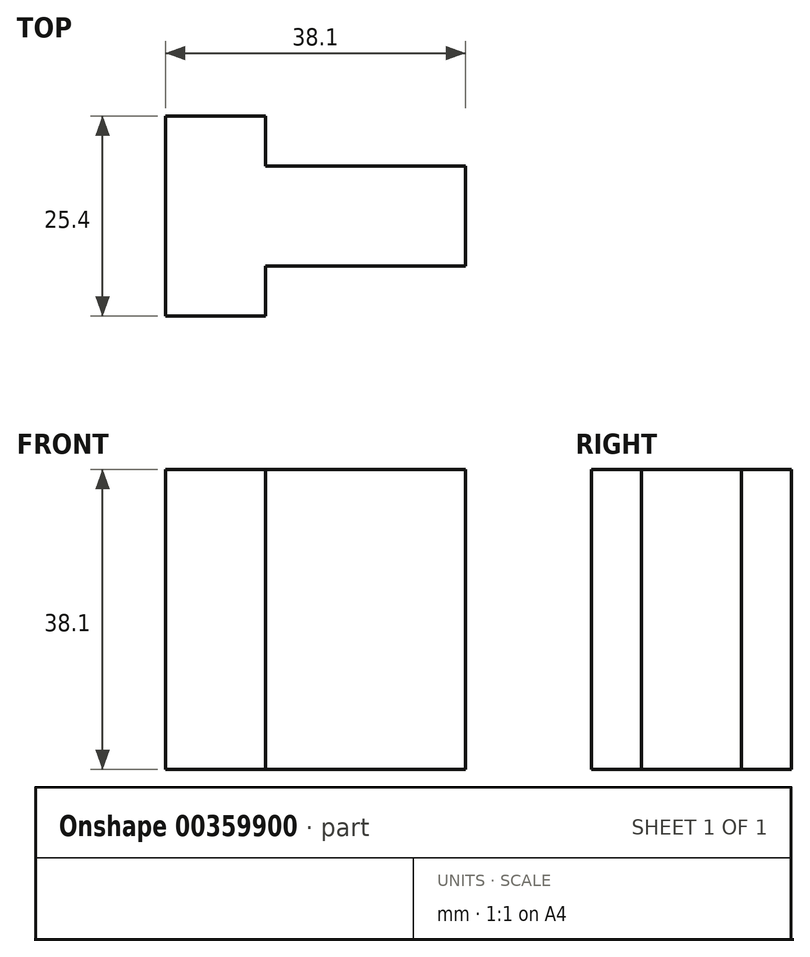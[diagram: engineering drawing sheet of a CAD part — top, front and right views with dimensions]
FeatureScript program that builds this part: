
annotation { "Feature Type Name" : "Feature", "Feature Type Description" : "" }
export const myFeature = defineFeature(function(context is Context, id is Id, definition is map)
    precondition{}
    {
        {
            var Q0;
            Q0=qCreatedBy(makeId("Top.planeOp"),FACE);
            var sketch = newSketch(context, id + "F0", { "sketchPlane" : qUnion([Q0])});
            skLineSegment(sketch, "E0", {"start": v(0, 0) * mm, "end": v(0, 25.4) * mm});
            skLineSegment(sketch, "E1", {"start": v(0, 25.4) * mm, "end": v(12.7, 25.4) * mm});
            skLineSegment(sketch, "E2", {"start": v(12.7, 25.4) * mm, "end": v(12.7, 19.05) * mm});
            skLineSegment(sketch, "E3", {"start": v(12.7, 19.05) * mm, "end": v(38.1, 19.05) * mm});
            skLineSegment(sketch, "E4", {"start": v(38.1, 19.05) * mm, "end": v(38.1, 6.35) * mm});
            skLineSegment(sketch, "E5", {"start": v(38.1, 6.35) * mm, "end": v(12.7, 6.35) * mm});
            skLineSegment(sketch, "E6", {"start": v(12.7, 6.35) * mm, "end": v(12.7, 0) * mm});
            skLineSegment(sketch, "E7", {"start": v(12.7, 0) * mm, "end": v(0, 0) * mm});
            skSolve(sketch);
        }
        {
            var Q0;
            Q0 = qSketchRegion(id + "F0", true);
            extrude(context, id + "F1", {"entities" : qUnion([Q0]), "depth" : 38.1 * mm});
        }
    });
